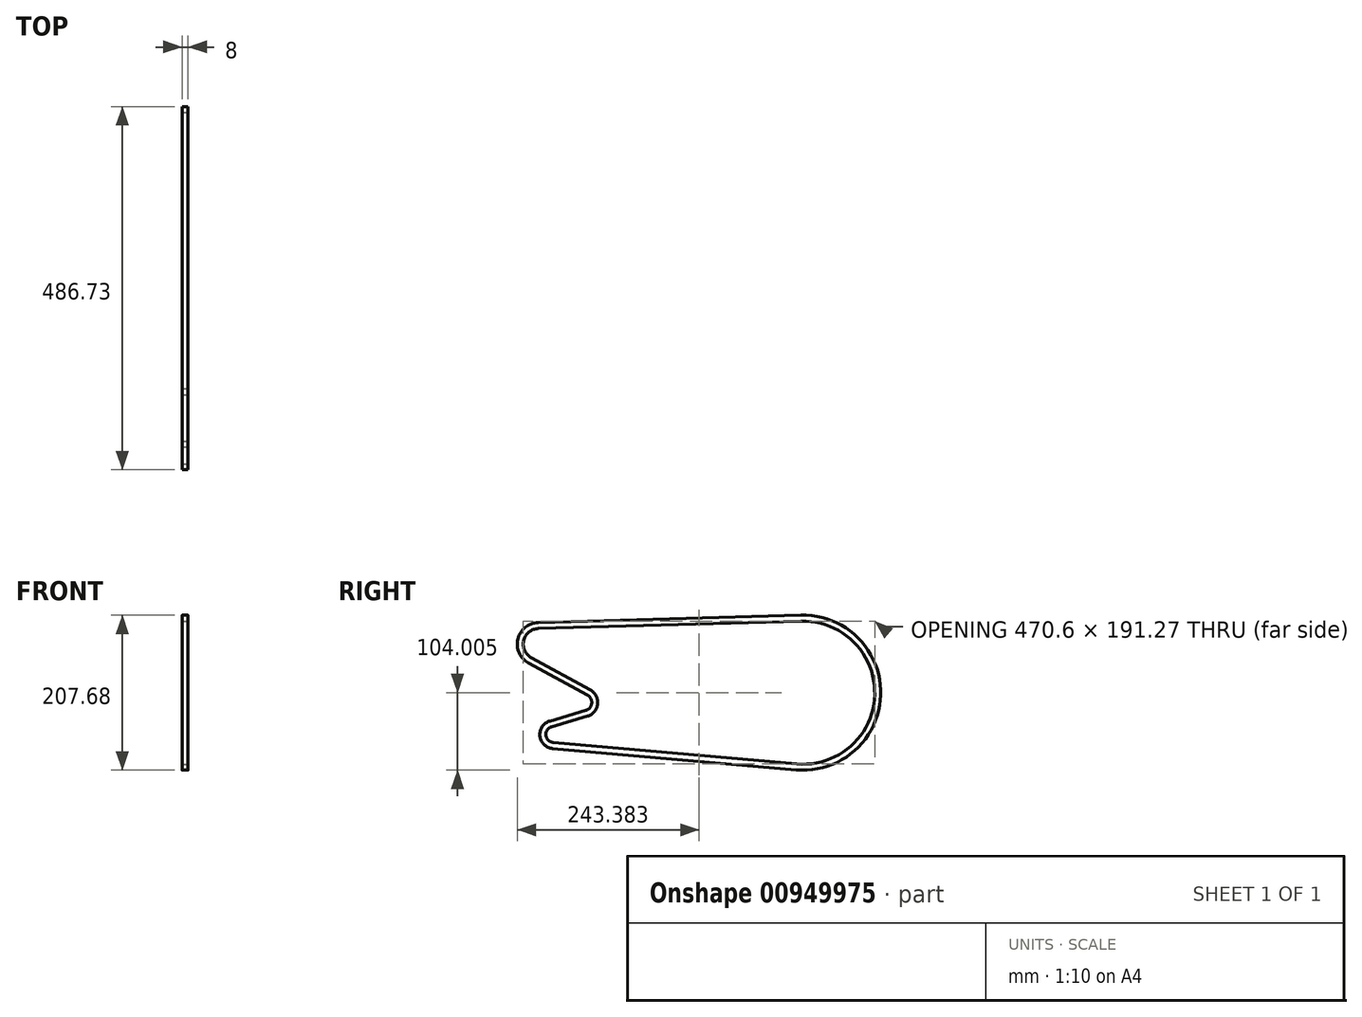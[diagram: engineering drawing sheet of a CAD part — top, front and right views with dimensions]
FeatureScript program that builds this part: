
annotation { "Feature Type Name" : "Feature", "Feature Type Description" : "" }
export const myFeature = defineFeature(function(context is Context, id is Id, definition is map)
    precondition{}
    {
        {
            var Q0;
            Q0=qCreatedBy(makeId("Right.planeOp"),FACE);
            var sketch = newSketch(context, id + "F0", { "sketchPlane" : qUnion([Q0])});
            skArc(sketch, "E0", {"start": v(-8.75, -99.62) * mm, "mid": v(99.96, -2.99) * mm, "end": v(-2.8, 99.96) * mm});
            skArc(sketch, "E1", {"start": v(-354.75, 90.14) * mm, "mid": v(-378.36, 71) * mm, "end": v(-366.06, 43.22) * mm});
            skLineSegment(sketch, "E2", {"start": v(-354.75, 90.14) * mm, "end": v(-2.8, 99.96) * mm});
            skPoint(sketch, "E3", {"position": v(-354.75, 90.14) * mm});
            skPoint(sketch, "E4", {"position": v(-366.06, 43.22) * mm});
            skPoint(sketch, "E5", {"position": v(-44.44, -89.58) * mm});
            skPoint(sketch, "E6", {"position": v(-2.8, 99.96) * mm});
            skArc(sketch, "E7", {"start": v(-290.1, -27.55) * mm, "mid": v(-279.4, -14.77) * mm, "end": v(-287.12, 0) * mm});
            skArc(sketch, "E8", {"start": v(-338, -41.6) * mm, "mid": v(-348.7, -57.48) * mm, "end": v(-335.09, -70.94) * mm});
            skLineSegment(sketch, "E9", {"start": v(-366.06, 43.22) * mm, "end": v(-287.12, 0) * mm});
            skLineSegment(sketch, "E10", {"start": v(-335.09, -70.94) * mm, "end": v(-8.75, -99.62) * mm});
            skLineSegment(sketch, "E11", {"start": v(-338, -41.6) * mm, "end": v(-290.1, -27.55) * mm});
            skSolve(sketch);
        }
        {
            var Q0;
            Q0=qCreatedBy(makeId("Front.planeOp"),FACE);
            var sketch = newSketch(context, id + "F1", { "sketchPlane" : qUnion([Q0])});
            skLineSegment(sketch, "E12.bottom", {"start": v(4, 103.84) * mm, "end": v(-4, 103.84) * mm});
            skLineSegment(sketch, "E12.top", {"start": v(4, 95.84) * mm, "end": v(-4, 95.84) * mm});
            skLineSegment(sketch, "E12.left", {"start": v(4, 103.84) * mm, "end": v(4, 95.84) * mm});
            skLineSegment(sketch, "E12.right", {"start": v(-4, 103.84) * mm, "end": v(-4, 95.84) * mm});
            skSolve(sketch);
        }
        {
            var Q0;
            Q0=makeQuery(id+"F1.imprint","IMPRINT",FACE,{"disambiguationData":[TD([[makeQuery(id+"F1.imprint","IMPRINT",EDGE,{"derivedFrom":sQuery(id+"F1.wireOp",EDGE,"E12.bottom")}),1.0]])]});
            var Q1;
            Q1=sQuery(id+"F0.wireOp",EDGE,"E2");
            var Q2;
            Q2=sQuery(id+"F0.wireOp",EDGE,"E0");
            var Q3;
            Q3=sQuery(id+"F0.wireOp",EDGE,"xD74B9uP-QXV6-qiwC-RsyW-5U2eyFzenrgA");
            var Q4;
            Q4=sQuery(id+"F0.wireOp",EDGE,"E1");
            var Q5;
            Q5=sQuery(id+"F0.wireOp",EDGE,"E9");
            var Q6;
            Q6=sQuery(id+"F0.wireOp",EDGE,"E7");
            var Q7;
            Q7=sQuery(id+"F0.wireOp",EDGE,"E11");
            var Q8;
            Q8=sQuery(id+"F0.wireOp",EDGE,"E8");
            var Q9;
            Q9=sQuery(id+"F0.wireOp",EDGE,"E10");
            sweep(context, id + "F2", {"profiles" : qUnion([Q0]), "path" : qUnion([Q1, Q2, Q3, Q4, Q5, Q6, Q7, Q8, Q9])});
        }
    });
